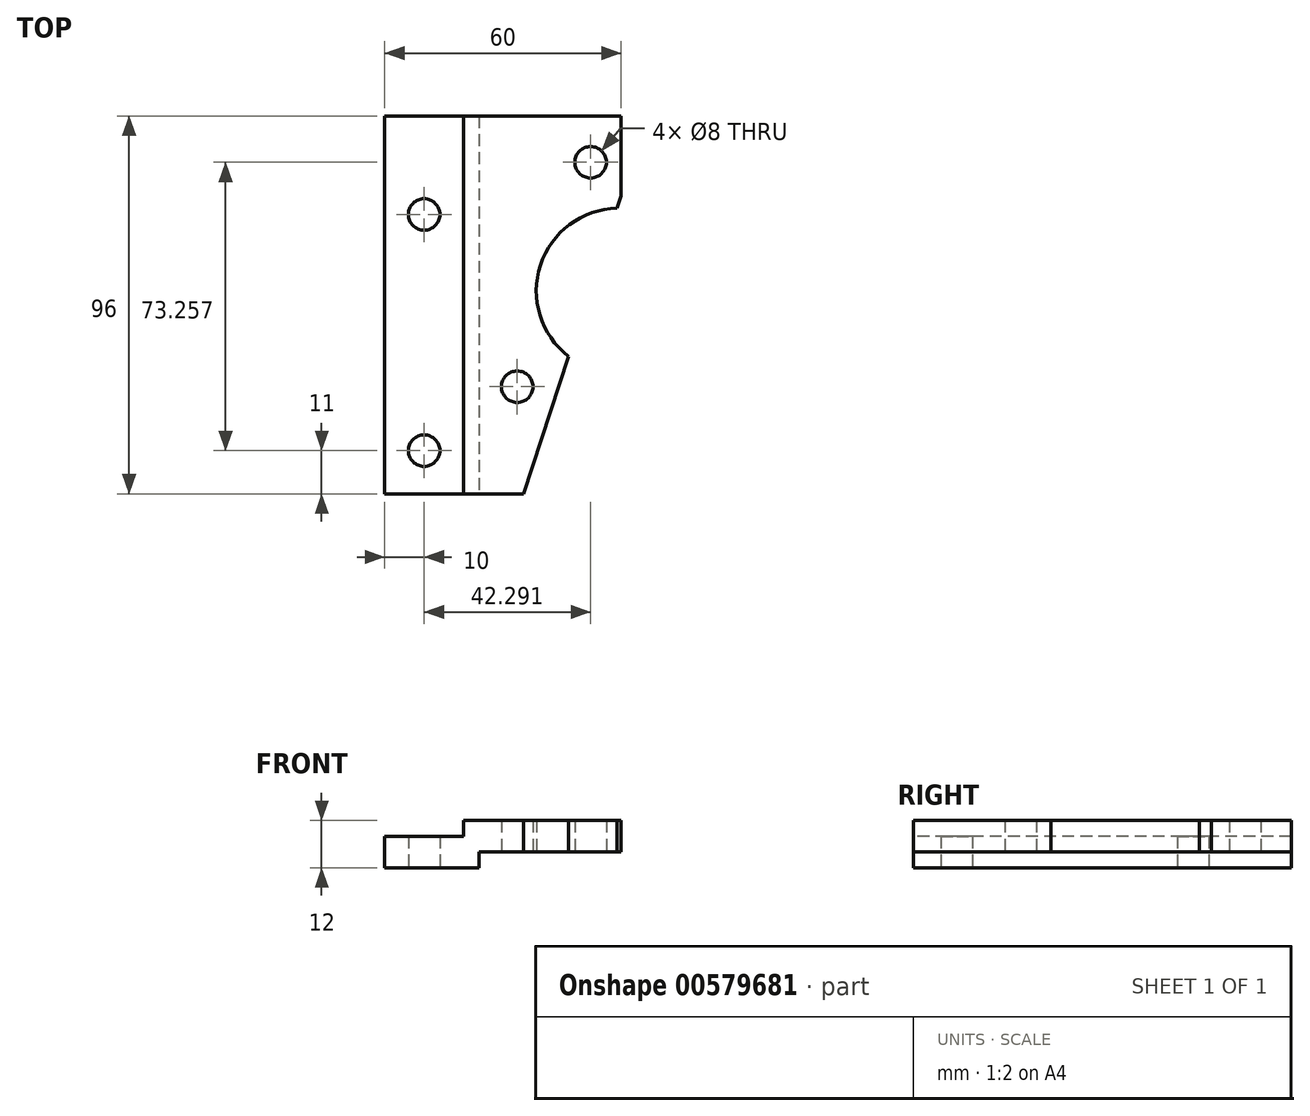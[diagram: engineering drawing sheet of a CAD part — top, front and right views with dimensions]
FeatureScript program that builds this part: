
annotation { "Feature Type Name" : "Feature", "Feature Type Description" : "" }
export const myFeature = defineFeature(function(context is Context, id is Id, definition is map)
    precondition{}
    {
        {
            var Q0;
            Q0=qCreatedBy(makeId("Top.planeOp"),FACE);
            var sketch = newSketch(context, id + "F0", { "sketchPlane" : qUnion([Q0])});
            skCircle(sketch, "E0", {"center": v(0, 0) * mm, "radius": 130 * mm});
            skCircle(sketch, "E1", {"center": v(42.3, 129.26) * mm, "radius": 4 * mm});
            skCircle(sketch, "E2", {"center": v(23.63, 72.23) * mm, "radius": 4 * mm});
            skCircle(sketch, "E3", {"center": v(49.49, 96.59) * mm, "radius": 21 * mm});
            skCircle(sketch, "E4", {"center": v(0, 0) * mm, "radius": 54 * mm});
            skLineSegment(sketch, "E5.bottom", {"start": v(50, 141) * mm, "end": v(-10, 141) * mm});
            skLineSegment(sketch, "E5.top", {"start": v(50, 45) * mm, "end": v(-10, 45) * mm});
            skLineSegment(sketch, "E5.left", {"start": v(50, 141) * mm, "end": v(50, 45) * mm});
            skLineSegment(sketch, "E5.right", {"start": v(-10, 141) * mm, "end": v(-10, 45) * mm});
            skCircle(sketch, "E6", {"center": v(0, 116) * mm, "radius": 4 * mm});
            skCircle(sketch, "E7", {"center": v(0, 56) * mm, "radius": 4 * mm});
            skLineSegment(sketch, "E8", {"start": v(10, 141) * mm, "end": v(10, 45) * mm});
            skLineSegment(sketch, "E9", {"start": v(0, 0) * mm, "end": v(42.3, 129.26) * mm});
            skLineSegment(sketch, "E10", {"start": v(64.57, 165.2) * mm, "end": v(14.42, 11.93) * mm});
            skLineSegment(sketch, "E11", {"start": v(14, 141) * mm, "end": v(14, 45) * mm});
            skSolve(sketch);
        }
        {
            var Q0;
            Q0=makeQuery(id+"F0.imprint","IMPRINT",FACE,{"disambiguationData":[TD([[makeQuery(id+"F0.imprint","IMPRINT",EDGE,{"derivedFrom":sQuery(id+"F0.wireOp",EDGE,"E1")}),-1.0]])]});
            var Q1;
            Q1=makeQuery(id+"F0.imprint","IMPRINT",FACE,{"disambiguationData":[TD([[makeQuery(id+"F0.imprint","IMPRINT",EDGE,{"derivedFrom":sQuery(id+"F0.wireOp",EDGE,"E2")}),-1.0]])]});
            var Q2;
            {var subQ3=sQuery(id+"F0.wireOp",EDGE,"E4");var subQ5=sQuery(id+"F0.wireOp",EDGE,"E7");var subQ8=makeQuery(id+"F0.imprint","INTERSECT",VERTEX,{"disambiguationData":[OD(0.0)],"derivedFrom":[subQ3,subQ5]});Q2=makeQuery(id+"F0.imprint","IMPRINT",FACE,{"disambiguationData":[TD([[makeQuery(id+"F0.imprint","IMPRINT",EDGE,{"disambiguationData":[TD([[subQ8,1.0]])],"derivedFrom":subQ3}),1.0]])]});}
            var Q3;
            {var subQ0=sQuery(id+"F0.wireOp",EDGE,"E5.right");var subQ1=sQuery(id+"F0.wireOp",EDGE,"E0");var subQ2=makeQuery(id+"F0.imprint","INTERSECT",VERTEX,{"derivedFrom":[subQ1,subQ0]});Q3=makeQuery(id+"F0.imprint","IMPRINT",FACE,{"disambiguationData":[TD([[makeQuery(id+"F0.imprint","IMPRINT",EDGE,{"disambiguationData":[TD([[subQ2,1.0]])],"derivedFrom":subQ1}),-1.0]])]});}
            var Q4;
            Q4=makeQuery(id+"F0.imprint","IMPRINT",FACE,{"disambiguationData":[TD([[makeQuery(id+"F0.imprint","IMPRINT",EDGE,{"derivedFrom":sQuery(id+"F0.wireOp",EDGE,"E6")}),-1.0]])]});
            var Q5;
            {var subQ0=sQuery(id+"F0.wireOp",EDGE,"E9");var subQ11=sQuery(id+"F0.wireOp",EDGE,"E0");var subQ12=makeQuery(id+"F0.imprint","INTERSECT",VERTEX,{"derivedFrom":[subQ11,subQ0]});Q5=makeQuery(id+"F0.imprint","IMPRINT",FACE,{"disambiguationData":[TD([[makeQuery(id+"F0.imprint","IMPRINT",EDGE,{"disambiguationData":[TD([[subQ12,-1.0]])],"derivedFrom":subQ11}),1.0]])]});}
            var Q6;
            {var subQ0=sQuery(id+"F0.wireOp",EDGE,"E9");var subQ1=sQuery(id+"F0.wireOp",EDGE,"E0");var subQ2=makeQuery(id+"F0.imprint","INTERSECT",VERTEX,{"derivedFrom":[subQ1,subQ0]});Q6=makeQuery(id+"F0.imprint","IMPRINT",FACE,{"disambiguationData":[TD([[makeQuery(id+"F0.imprint","IMPRINT",EDGE,{"disambiguationData":[TD([[subQ2,1.0]])],"derivedFrom":subQ1}),1.0]])]});}
            var Q7;
            {var subQ0=sQuery(id+"F0.wireOp",EDGE,"E10");var subQ1=sQuery(id+"F0.wireOp",EDGE,"E4");var subQ2=makeQuery(id+"F0.imprint","INTERSECT",VERTEX,{"derivedFrom":[subQ1,subQ0]});Q7=makeQuery(id+"F0.imprint","IMPRINT",FACE,{"disambiguationData":[TD([[makeQuery(id+"F0.imprint","IMPRINT",EDGE,{"disambiguationData":[TD([[subQ2,-1.0]])],"derivedFrom":subQ1}),1.0]])]});}
            var Q8;
            {var subQ0=sQuery(id+"F0.wireOp",EDGE,"E9");var subQ1=sQuery(id+"F0.wireOp",EDGE,"E4");var subQ2=makeQuery(id+"F0.imprint","INTERSECT",VERTEX,{"derivedFrom":[subQ1,subQ0]});Q8=makeQuery(id+"F0.imprint","IMPRINT",FACE,{"disambiguationData":[TD([[makeQuery(id+"F0.imprint","IMPRINT",EDGE,{"disambiguationData":[TD([[subQ2,-1.0]])],"derivedFrom":subQ1}),1.0]])]});}
            var Q9;
            {var subQ0=sQuery(id+"F0.wireOp",EDGE,"E11");var subQ1=sQuery(id+"F0.wireOp",EDGE,"E0");var subQ2=makeQuery(id+"F0.imprint","INTERSECT",VERTEX,{"derivedFrom":[subQ1,subQ0]});Q9=makeQuery(id+"F0.imprint","IMPRINT",FACE,{"disambiguationData":[TD([[makeQuery(id+"F0.imprint","IMPRINT",EDGE,{"disambiguationData":[TD([[subQ2,-1.0]])],"derivedFrom":subQ1}),-1.0]])]});}
            var Q10;
            {var subQ0=sQuery(id+"F0.wireOp",EDGE,"E11");var subQ1=sQuery(id+"F0.wireOp",EDGE,"E0");var subQ2=makeQuery(id+"F0.imprint","INTERSECT",VERTEX,{"derivedFrom":[subQ1,subQ0]});Q10=makeQuery(id+"F0.imprint","IMPRINT",FACE,{"disambiguationData":[TD([[makeQuery(id+"F0.imprint","IMPRINT",EDGE,{"disambiguationData":[TD([[subQ2,-1.0]])],"derivedFrom":subQ1}),1.0]])]});}
            var Q11;
            {var subQ0=sQuery(id+"F0.wireOp",EDGE,"E11");var subQ1=sQuery(id+"F0.wireOp",EDGE,"E4");var subQ2=makeQuery(id+"F0.imprint","INTERSECT",VERTEX,{"derivedFrom":[subQ1,subQ0]});Q11=makeQuery(id+"F0.imprint","IMPRINT",FACE,{"disambiguationData":[TD([[makeQuery(id+"F0.imprint","IMPRINT",EDGE,{"disambiguationData":[TD([[subQ2,-1.0]])],"derivedFrom":subQ1}),1.0]])]});}
            extrude(context, id + "F1", {"entities" : qUnion([Q0, Q1, Q2, Q3, Q4, Q5, Q6, Q7, Q8, Q9, Q10, Q11]), "endBound" : BoundingType.SYMMETRIC, "depth" : 12 * mm, "offsetDistance" : 25 * mm});
        }
        {
            var Q0;
            Q0=makeQuery(id+"F1.opExtrude","CAP_FACE",FACE,{"disambiguationData":[OSD([sQuery(id+"F0.wireOp",EDGE,"E1"),sQuery(id+"F0.wireOp",EDGE,"E2"),sQuery(id+"F0.wireOp",EDGE,"E3"),sQuery(id+"F0.wireOp",EDGE,"E5.bottom"),sQuery(id+"F0.wireOp",EDGE,"E5.top"),sQuery(id+"F0.wireOp",EDGE,"E5.left"),sQuery(id+"F0.wireOp",EDGE,"E5.right"),sQuery(id+"F0.wireOp",EDGE,"E6"),sQuery(id+"F0.wireOp",EDGE,"E7"),sQuery(id+"F0.wireOp",EDGE,"E10")])],"isStart":false});
            var sketch = newSketch(context, id + "F2", { "sketchPlane" : qUnion([Q0])});
            skLineSegment(sketch, "E12.bottom", {"start": v(10.04, 45) * mm, "end": v(-10, 45) * mm});
            skLineSegment(sketch, "E12.top", {"start": v(10.04, 141) * mm, "end": v(-10, 141) * mm});
            skLineSegment(sketch, "E12.left", {"start": v(10.04, 45) * mm, "end": v(10.04, 141) * mm});
            skLineSegment(sketch, "E12.right", {"start": v(-10, 45) * mm, "end": v(-10, 141) * mm});
            skSolve(sketch);
        }
        {
            var Q0;
            Q0=makeQuery(id+"F2.imprint","IMPRINT",FACE,{"disambiguationData":[TD([[makeQuery(id+"F2.imprint","IMPRINT",EDGE,{"derivedFrom":sQuery(id+"F2.wireOp",EDGE,"E12.bottom")}),-1.0]])]});
            extrude(context, id + "F3", {"entities" : qUnion([Q0]), "operationType" : NewBodyOperationType.REMOVE, "endBound" : BoundingType.SYMMETRIC, "oppositeDirection" : true, "depth" : 8 * mm, "offsetDistance" : 25 * mm});
        }
        {
            var Q0;
            Q0=makeQuery(id+"F1.opExtrude","CAP_FACE",FACE,{"disambiguationData":[OSD([sQuery(id+"F0.wireOp",EDGE,"E1"),sQuery(id+"F0.wireOp",EDGE,"E2"),sQuery(id+"F0.wireOp",EDGE,"E3"),sQuery(id+"F0.wireOp",EDGE,"E5.bottom"),sQuery(id+"F0.wireOp",EDGE,"E5.top"),sQuery(id+"F0.wireOp",EDGE,"E5.left"),sQuery(id+"F0.wireOp",EDGE,"E5.right"),sQuery(id+"F0.wireOp",EDGE,"E6"),sQuery(id+"F0.wireOp",EDGE,"E7"),sQuery(id+"F0.wireOp",EDGE,"E10")])],"isStart":true});
            var sketch = newSketch(context, id + "F4", { "sketchPlane" : qUnion([Q0])});
            skLineSegment(sketch, "E13.bottom", {"start": v(50, -141) * mm, "end": v(13.97, -141) * mm});
            skLineSegment(sketch, "E13.top", {"start": v(50, -45) * mm, "end": v(13.97, -45) * mm});
            skLineSegment(sketch, "E13.left", {"start": v(50, -141) * mm, "end": v(50, -45) * mm});
            skLineSegment(sketch, "E13.right", {"start": v(13.97, -141) * mm, "end": v(13.97, -45) * mm});
            skSolve(sketch);
        }
        {
            var Q0;
            {var subQ1=sQuery(id+"F4.wireOp",EDGE,"E13.bottom");Q0=makeQuery(id+"F4.imprint","IMPRINT",FACE,{"disambiguationData":[TD([[makeQuery(id+"F4.imprint","IMPRINT",EDGE,{"derivedFrom":subQ1}),-1.0]])]});}
            extrude(context, id + "F5", {"entities" : qUnion([Q0]), "operationType" : NewBodyOperationType.REMOVE, "oppositeDirection" : true, "depth" : 4 * mm, "offsetDistance" : 25 * mm});
        }
    });
